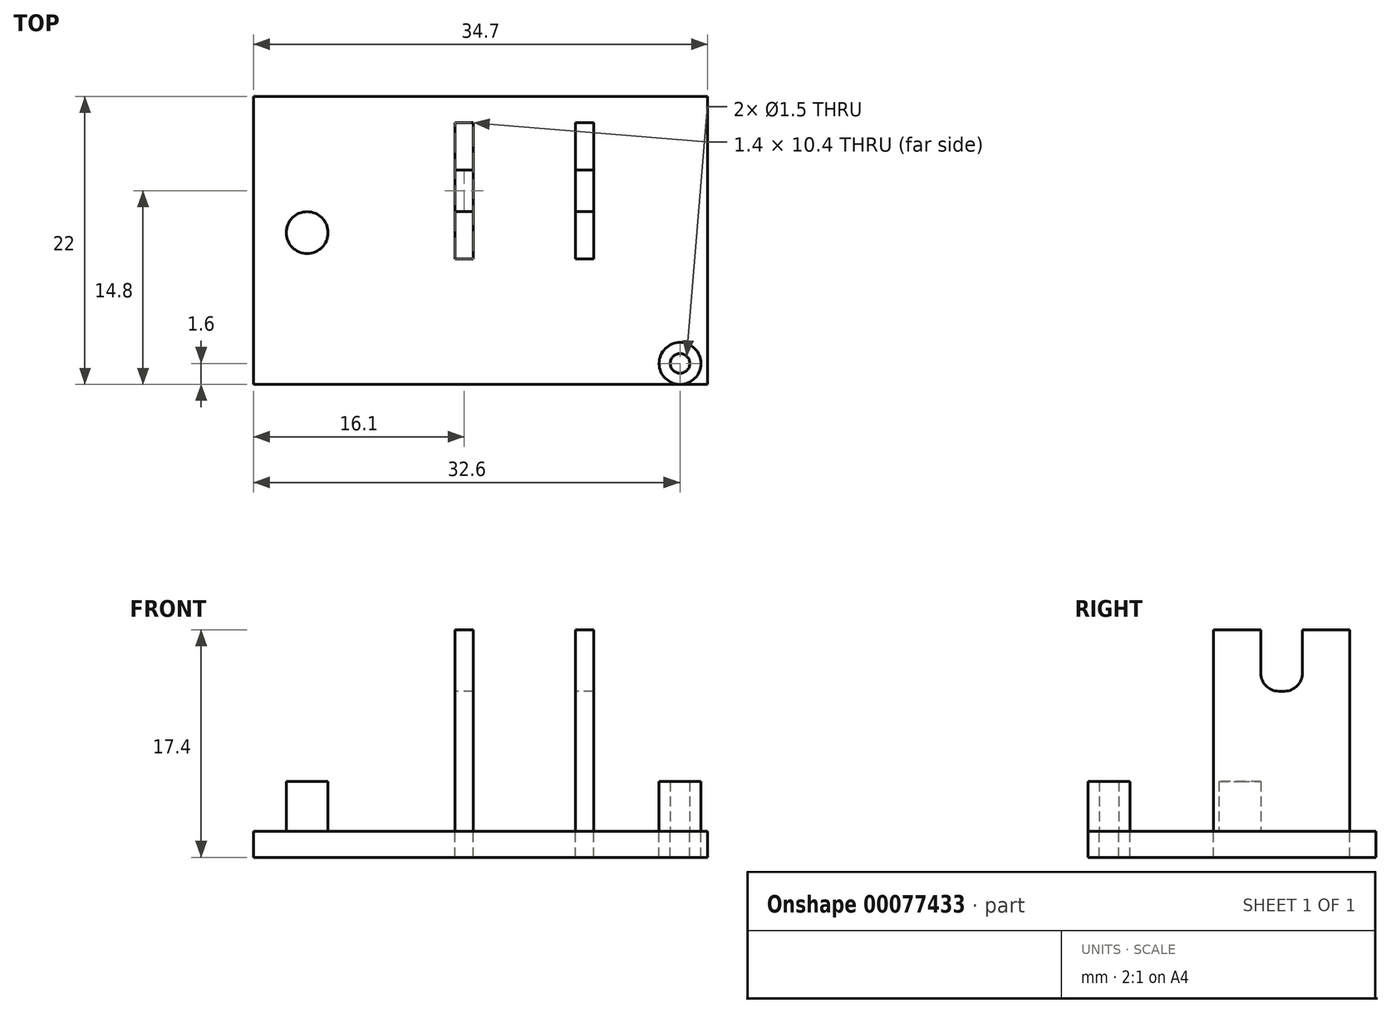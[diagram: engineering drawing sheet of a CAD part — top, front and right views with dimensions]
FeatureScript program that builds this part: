
annotation { "Feature Type Name" : "Feature", "Feature Type Description" : "" }
export const myFeature = defineFeature(function(context is Context, id is Id, definition is map)
    precondition{}
    {
        {
            var Q0;
            Q0=qCreatedBy(makeId("Top.planeOp"),FACE);
            var sketch = newSketch(context, id + "F0", { "sketchPlane" : qUnion([Q0])});
            skLineSegment(sketch, "E0.rect.bottom", {"start": v(-20.7, 11) * mm, "end": v(14, 11) * mm});
            skLineSegment(sketch, "E0.rect.top", {"start": v(-20.7, -11) * mm, "end": v(14, -11) * mm});
            skLineSegment(sketch, "E0.rect.right", {"start": v(14, 11) * mm, "end": v(14, -11) * mm});
            skPoint(sketch, "E0.rect.middle", {"position": v(0, 0) * mm});
            skLineSegment(sketch, "E1.rect.bottom", {"start": v(5.3, -1.4) * mm, "end": v(-5.3, -1.4) * mm, "construction": true});
            skLineSegment(sketch, "E1.rect.top", {"start": v(5.3, 9) * mm, "end": v(-5.3, 9) * mm, "construction": true});
            skLineSegment(sketch, "E1.rect.left", {"start": v(5.3, -1.4) * mm, "end": v(5.3, 9) * mm, "construction": true});
            skLineSegment(sketch, "E1.rect.right", {"start": v(-5.3, -1.4) * mm, "end": v(-5.3, 9) * mm, "construction": true});
            skPoint(sketch, "E1.rect.middle", {"position": v(0, 3.8) * mm});
            skLineSegment(sketch, "E2.bottom", {"start": v(-5.3, 9) * mm, "end": v(-3.9, 9) * mm});
            skLineSegment(sketch, "E2.top", {"start": v(-5.3, -1.4) * mm, "end": v(-3.9, -1.4) * mm});
            skLineSegment(sketch, "E2.left", {"start": v(-5.3, 9) * mm, "end": v(-5.3, -1.4) * mm});
            skLineSegment(sketch, "E2.right", {"start": v(-3.9, 9) * mm, "end": v(-3.9, -1.4) * mm});
            skLineSegment(sketch, "E3.1.MirrorCS", {"start": v(3.9, 9) * mm, "end": v(3.9, -1.4) * mm});
            skLineSegment(sketch, "E3.2.MirrorCS", {"start": v(5.3, -1.4) * mm, "end": v(3.9, -1.4) * mm});
            skLineSegment(sketch, "E3.3.MirrorCS", {"start": v(5.3, 9) * mm, "end": v(5.3, -1.4) * mm});
            skLineSegment(sketch, "E3.4.MirrorCS", {"start": v(5.3, 9) * mm, "end": v(3.9, 9) * mm});
            skLineSegment(sketch, "E4", {"start": v(11.9, -2.52) * mm, "end": v(11.9, -9.66) * mm, "construction": true});
            skLineSegment(sketch, "E5", {"start": v(3.95, -9.4) * mm, "end": v(12.65, -9.4) * mm, "construction": true});
            skLineSegment(sketch, "E6", {"start": v(5.3, 3.8) * mm, "end": v(11.55, 3.8) * mm, "construction": true});
            skCircle(sketch, "E7", {"center": v(11.9, -9.4) * mm, "radius": 1.6 * mm});
            skCircle(sketch, "E8", {"center": v(11.9, -9.4) * mm, "radius": 0.75 * mm});
            skLineSegment(sketch, "E9", {"start": v(-16.6, 8.88) * mm, "end": v(-16.6, 1.47) * mm, "construction": true});
            skLineSegment(sketch, "E10", {"start": v(-16.6, 1.47) * mm, "end": v(-16.6, -2.71) * mm, "construction": true});
            skLineSegment(sketch, "E11", {"start": v(-17.93, 0.6) * mm, "end": v(-7.68, 0.6) * mm, "construction": true});
            skCircle(sketch, "E12", {"center": v(-16.6, 0.6) * mm, "radius": 1.6 * mm});
            skCircle(sketch, "E13", {"center": v(-16.6, 0.6) * mm, "radius": 0.45 * mm});
            skLineSegment(sketch, "E14", {"start": v(-20.7, 11) * mm, "end": v(-20.7, -11) * mm});
            skPoint(sketch, "E15.orphan", {"position": v(-14, -11) * mm});
            skPoint(sketch, "E0.rect.left.start.orphan", {"position": v(-14, 11) * mm});
            skSolve(sketch);
        }
        {
            var Q0;
            Q0=makeQuery(id+"F0.imprint","IMPRINT",FACE,{"disambiguationData":[TD([[makeQuery(id+"F0.imprint","IMPRINT",EDGE,{"derivedFrom":sQuery(id+"F0.wireOp",EDGE,"E2.bottom")}),-1.0]])]});
            var Q1;
            Q1=makeQuery(id+"F0.imprint","IMPRINT",FACE,{"disambiguationData":[TD([[makeQuery(id+"F0.imprint","IMPRINT",EDGE,{"derivedFrom":sQuery(id+"F0.wireOp",EDGE,"E3.1.MirrorCS")}),1.0]])]});
            extrude(context, id + "F1", {"entities" : qUnion([Q0, Q1]), "depth" : 15.4 * mm});
        }
        {
            var Q0;
            Q0=makeQuery(id+"F0.imprint","IMPRINT",FACE,{"disambiguationData":[TD([[makeQuery(id+"F0.imprint","IMPRINT",EDGE,{"derivedFrom":sQuery(id+"F0.wireOp",EDGE,"E12")}),1.0]])]});
            var Q1;
            Q1=makeQuery(id+"F0.imprint","IMPRINT",FACE,{"disambiguationData":[TD([[makeQuery(id+"F0.imprint","IMPRINT",EDGE,{"derivedFrom":sQuery(id+"F0.wireOp",EDGE,"E7")}),1.0]])]});
            var Q2;
            Q2=makeQuery(id+"F0.imprint","IMPRINT",FACE,{"disambiguationData":[TD([[makeQuery(id+"F0.imprint","IMPRINT",EDGE,{"derivedFrom":sQuery(id+"F0.wireOp",EDGE,"E13")}),1.0]])]});
            extrude(context, id + "F2", {"entities" : qUnion([Q0, Q1, Q2]), "depth" : 3.8 * mm});
        }
        {
            var Q0;
            Q0=sQuery(id+"F0.wireOp",EDGE,"E13");
            extrude(context, id + "F3", {"bodyType" : ToolBodyType.SURFACE, "surfaceEntities" : qUnion([Q0]), "depth" : 4.8 * mm});
        }
        {
            var Q0;
            Q0=makeQuery(id+"F1.opExtrude","SWEPT_FACE",FACE,{"disambiguationData":[OSD([sQuery(id+"F0.wireOp",EDGE,"E2.left")])]});
            var sketch = newSketch(context, id + "F4", { "sketchPlane" : qUnion([Q0])});
            skLineSegment(sketch, "E16", {"start": v(-3.8, 15.4) * mm, "end": v(-3.8, 9.08) * mm, "construction": true});
            skLineSegment(sketch, "E17", {"start": v(-5.38, 15.4) * mm, "end": v(-5.38, 12.05) * mm});
            skLineSegment(sketch, "E18.0.MirrorCS", {"start": v(-2.22, 15.4) * mm, "end": v(-2.22, 12.05) * mm});
            skLineSegment(sketch, "E19", {"start": v(-4.03, 10.7) * mm, "end": v(-3.57, 10.7) * mm});
            skPoint(sketch, "E20.newPointA", {"position": v(-5.38, 9) * mm});
            skArc(sketch, "E20.filletArc", {"start": v(-5.38, 12.05) * mm, "mid": v(-4.98, 11.1) * mm, "end": v(-4.03, 10.7) * mm});
            skPoint(sketch, "E21.newPointB", {"position": v(-2.22, 9) * mm});
            skArc(sketch, "E21.filletArc", {"start": v(-3.57, 10.7) * mm, "mid": v(-2.62, 11.1) * mm, "end": v(-2.22, 12.05) * mm});
            skSolve(sketch);
        }
        {
            var Q0;
            Q0=makeQuery(id+"F0.imprint","IMPRINT",FACE,{"disambiguationData":[TD([[makeQuery(id+"F0.imprint","IMPRINT",EDGE,{"derivedFrom":sQuery(id+"F0.wireOp",EDGE,"E0.rect.bottom")}),-1.0]])]});
            var Q1;
            Q1=makeQuery(id+"F0.imprint","IMPRINT",FACE,{"disambiguationData":[TD([[makeQuery(id+"F0.imprint","IMPRINT",EDGE,{"derivedFrom":sQuery(id+"F0.wireOp",EDGE,"E12")}),1.0]])]});
            var Q2;
            Q2=makeQuery(id+"F0.imprint","IMPRINT",FACE,{"disambiguationData":[TD([[makeQuery(id+"F0.imprint","IMPRINT",EDGE,{"derivedFrom":sQuery(id+"F0.wireOp",EDGE,"E13")}),1.0]])]});
            var Q3;
            Q3=makeQuery(id+"F0.imprint","IMPRINT",FACE,{"disambiguationData":[TD([[makeQuery(id+"F0.imprint","IMPRINT",EDGE,{"derivedFrom":sQuery(id+"F0.wireOp",EDGE,"E7")}),1.0]])]});
            var Q4;
            Q4=makeQuery(id+"F0.imprint","IMPRINT",FACE,{"disambiguationData":[TD([[makeQuery(id+"F0.imprint","IMPRINT",EDGE,{"derivedFrom":sQuery(id+"F0.wireOp",EDGE,"E8")}),1.0]])]});
            var Q5;
            Q5=makeQuery(id+"F2.opExtrude","CAP_FACE",FACE,{"disambiguationData":[OSD([sQuery(id+"F0.wireOp",EDGE,"E7"),sQuery(id+"F0.wireOp",EDGE,"E8")])],"isStart":true});
            var Q6;
            Q6=makeQuery(id+"F0.imprint","IMPRINT",FACE,{"disambiguationData":[TD([[makeQuery(id+"F0.imprint","IMPRINT",EDGE,{"derivedFrom":sQuery(id+"F0.wireOp",EDGE,"E3.1.MirrorCS")}),1.0]])]});
            var Q7;
            Q7=makeQuery(id+"F1.opExtrude","CAP_FACE",FACE,{"disambiguationData":[OSD([sQuery(id+"F0.wireOp",EDGE,"E3.1.MirrorCS"),sQuery(id+"F0.wireOp",EDGE,"E3.2.MirrorCS"),sQuery(id+"F0.wireOp",EDGE,"E3.3.MirrorCS"),sQuery(id+"F0.wireOp",EDGE,"E3.4.MirrorCS")])],"isStart":true});
            extrude(context, id + "F5", {"entities" : qUnion([Q0, Q1, Q2, Q3, Q4, Q5, Q6, Q7]), "oppositeDirection" : true, "depth" : 2 * mm});
        }
        {
            var Q0;
            {var subQ2=sQuery(id+"F4.wireOp",EDGE,"E17");Q0=makeQuery(id+"F4.imprint","IMPRINT",FACE,{"disambiguationData":[TD([[makeQuery(id+"F4.imprint","IMPRINT",EDGE,{"derivedFrom":subQ2}),1.0]])]});}
            extrude(context, id + "F6", {"entities" : qUnion([Q0]), "operationType" : NewBodyOperationType.REMOVE, "endBound" : BoundingType.THROUGH_ALL, "oppositeDirection" : true, "depth" : 25 * mm});
        }
    });
